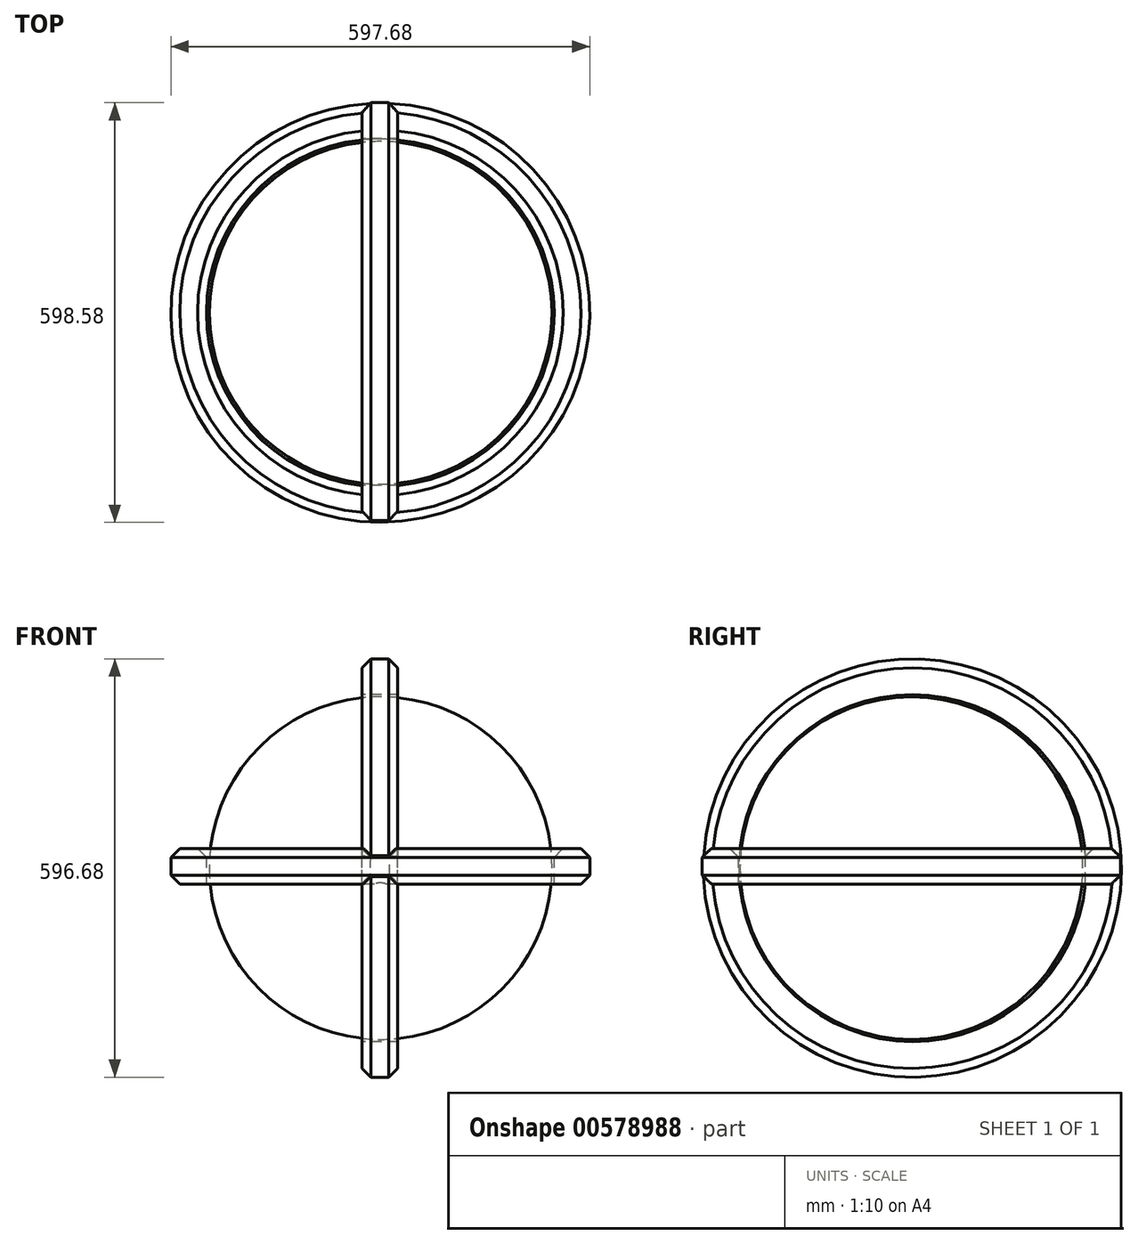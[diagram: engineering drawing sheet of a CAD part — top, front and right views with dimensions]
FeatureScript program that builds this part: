
annotation { "Feature Type Name" : "Feature", "Feature Type Description" : "" }
export const myFeature = defineFeature(function(context is Context, id is Id, definition is map)
    precondition{}
    {
        {
            var Q0;
            Q0=qCreatedBy(makeId("Right.planeOp"),FACE);
            var sketch = newSketch(context, id + "F0", { "sketchPlane" : qUnion([Q0])});
            skLineSegment(sketch, "E0", {"start": v(0, 17.4) * mm, "end": v(0, 0) * mm});
            skLineSegment(sketch, "E1", {"start": v(0, 0) * mm, "end": v(0, -17.12) * mm});
            skLineSegment(sketch, "E2.bottom", {"start": v(248.04, 28.12) * mm, "end": v(298.84, 28.12) * mm});
            skLineSegment(sketch, "E2.top", {"start": v(248.04, -22.68) * mm, "end": v(298.84, -22.68) * mm});
            skLineSegment(sketch, "E2.left", {"start": v(248.04, 28.12) * mm, "end": v(248.04, -22.68) * mm});
            skLineSegment(sketch, "E2.right", {"start": v(298.84, 28.12) * mm, "end": v(298.84, -22.68) * mm});
            skSolve(sketch);
        }
        {
            var Q0;
            Q0=makeQuery(id+"F0.imprint","IMPRINT",FACE,{"disambiguationData":[TD([[makeQuery(id+"F0.imprint","IMPRINT",EDGE,{"derivedFrom":sQuery(id+"F0.wireOp",EDGE,"E2.bottom")}),-1.0]])]});
            var Q1;
            Q1=sQuery(id+"F0.wireOp",EDGE,"E1");
            revolve(context, id + "F1", {"entities" : qUnion([Q0]), "axis" : qUnion([Q1]), "revolveType" : RevolveType.FULL});
        }
        {
            var Q0;
            Q0=makeQuery(id+"F1.opRevolve","SWEPT_FACE",FACE,{"disambiguationData":[OSD([sQuery(id+"F0.wireOp",EDGE,"E2.bottom")])]});
            chamfer(context, id + "F2", {"entities" : qUnion([Q0]), "width" : 12.7 * mm, "tangentPropagation" : true});
        }
        {
            var Q0;
            Q0=qCreatedBy(makeId("Front.planeOp"),FACE);
            var sketch = newSketch(context, id + "F3", { "sketchPlane" : qUnion([Q0])});
            skLineSegment(sketch, "E3.bottom", {"start": v(44.13, 8.1) * mm, "end": v(-49.52, 8.1) * mm});
            skLineSegment(sketch, "E3.top", {"start": v(44.13, -5.9) * mm, "end": v(-49.52, -5.9) * mm});
            skLineSegment(sketch, "E3.left", {"start": v(44.13, 8.1) * mm, "end": v(44.13, -5.9) * mm});
            skLineSegment(sketch, "E3.right", {"start": v(-49.52, 8.1) * mm, "end": v(-49.52, -5.9) * mm});
            skSolve(sketch);
        }
        {
            var Q0;
            Q0=qCreatedBy(makeId("Top.planeOp"),FACE);
            var sketch = newSketch(context, id + "F4", { "sketchPlane" : qUnion([Q0])});
            skCircle(sketch, "E4", {"center": v(0.4, -0.03) * mm, "radius": 244.39 * mm});
            skLineSegment(sketch, "E5", {"start": v(-244, -0.03) * mm, "end": v(244.79, -0.03) * mm});
            skSolve(sketch);
        }
        {
            var Q0;
            {var subQ0=sQuery(id+"F4.wireOp",EDGE,"E5");Q0=makeQuery(id+"F4.imprint","IMPRINT",FACE,{"disambiguationData":[TD([[makeQuery(id+"F4.imprint","IMPRINT",EDGE,{"derivedFrom":subQ0}),-1.0]])]});}
            var Q1;
            Q1=sQuery(id+"F4.wireOp",EDGE,"E5");
            revolve(context, id + "F5", {"operationType" : NewBodyOperationType.ADD, "entities" : qUnion([Q0]), "axis" : qUnion([Q1]), "revolveType" : RevolveType.FULL});
        }
        {
            var Q0;
            Q0=qCreatedBy(makeId("Top.planeOp"),FACE);
            var sketch = newSketch(context, id + "F6", { "sketchPlane" : qUnion([Q0])});
            skLineSegment(sketch, "E6.bottom", {"start": v(-26.02, 299.74) * mm, "end": v(24.78, 299.74) * mm});
            skLineSegment(sketch, "E6.top", {"start": v(-26.02, 248.94) * mm, "end": v(24.78, 248.94) * mm});
            skLineSegment(sketch, "E6.left", {"start": v(-26.02, 299.74) * mm, "end": v(-26.02, 248.94) * mm});
            skLineSegment(sketch, "E6.right", {"start": v(24.78, 299.74) * mm, "end": v(24.78, 248.94) * mm});
            skLineSegment(sketch, "E7", {"start": v(-0.45, 1.4) * mm, "end": v(57.21, 1.4) * mm});
            skLineSegment(sketch, "E8", {"start": v(-0.45, 1.4) * mm, "end": v(-65.41, 1.4) * mm});
            skSolve(sketch);
        }
        {
            var Q0;
            Q0=makeQuery(id+"F6.imprint","IMPRINT",FACE,{"disambiguationData":[TD([[makeQuery(id+"F6.imprint","IMPRINT",EDGE,{"derivedFrom":sQuery(id+"F6.wireOp",EDGE,"E6.bottom")}),-1.0]])]});
            var Q1;
            Q1=sQuery(id+"F6.wireOp",EDGE,"E7");
            revolve(context, id + "F7", {"operationType" : NewBodyOperationType.ADD, "entities" : qUnion([Q0]), "axis" : qUnion([Q1]), "revolveType" : RevolveType.FULL});
        }
        {
            var Q0;
            Q0=makeQuery(id+"F7.opRevolve","SWEPT_EDGE",EDGE,{"disambiguationData":[OSD([sQuery(id+"F6.wireOp",EDGE,"E6.bottom"),sQuery(id+"F6.wireOp",EDGE,"E6.left")])]});
            chamfer(context, id + "F8", {"entities" : qUnion([Q0]), "width" : 12.7 * mm, "tangentPropagation" : true});
        }
        {
            var Q0;
            Q0=makeQuery(id+"F1.opRevolve","SWEPT_EDGE",EDGE,{"disambiguationData":[OSD([sQuery(id+"F0.wireOp",EDGE,"E2.top"),sQuery(id+"F0.wireOp",EDGE,"E2.right")])]});
            chamfer(context, id + "F9", {"entities" : qUnion([Q0]), "width" : 12.7 * mm, "tangentPropagation" : true});
        }
        {
            var Q0;
            Q0=makeQuery(id+"F7.opRevolve","SWEPT_EDGE",EDGE,{"disambiguationData":[OSD([sQuery(id+"F6.wireOp",EDGE,"E6.bottom"),sQuery(id+"F6.wireOp",EDGE,"E6.right")])]});
            chamfer(context, id + "F10", {"entities" : qUnion([Q0]), "width" : 12.7 * mm, "tangentPropagation" : true});
        }
    });
